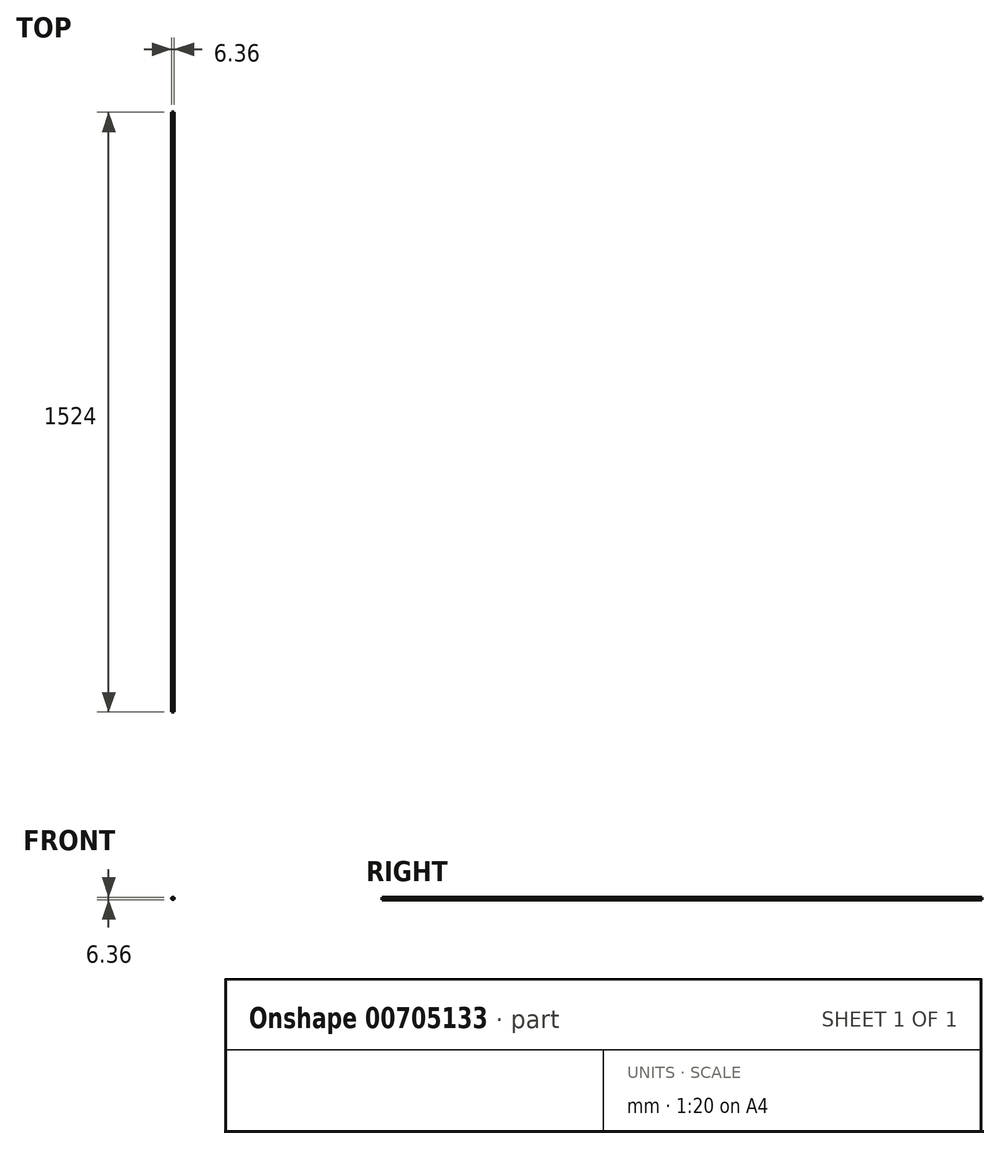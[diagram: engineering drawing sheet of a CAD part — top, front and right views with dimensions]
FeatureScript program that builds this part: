
annotation { "Feature Type Name" : "Feature", "Feature Type Description" : "" }
export const myFeature = defineFeature(function(context is Context, id is Id, definition is map)
    precondition{}
    {
        {
            var Q0;
            Q0=qCreatedBy(makeId("Front.planeOp"),FACE);
            var sketch = newSketch(context, id + "F0", { "sketchPlane" : qUnion([Q0])});
            skCircle(sketch, "E0", {"center": v(0, 0) * mm, "radius": 3.18 * mm});
            skSolve(sketch);
        }
        {
            var Q0;
            Q0 = qSketchRegion(id + "F0", true);
            extrude(context, id + "F1", {"entities" : qUnion([Q0]), "depth" : 1524 * mm, "offsetDistance" : 25.4 * mm});
        }
    });
